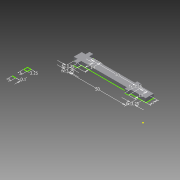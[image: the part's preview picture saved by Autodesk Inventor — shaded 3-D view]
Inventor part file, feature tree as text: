
AUTODESK INVENTOR PART (.ipt)
format: ipt  version: 2013 (Build 170138000, 138)  size: 106,496 bytes
history: native  units: mm
features: extrude x2, sketch x1
ambient origin geometry x8: Origin, YZ Plane, XZ Plane, XY Plane, X Axis, Y Axis, Z Axis, Center Point
feature tree (3):
  sketch  "Sketch1"  dims[d3=3.0mm d5=3.0mm d44=3.25mm d45=14.0mm d46=3.25mm d47=7.0mm d48=50.0mm d49=3.25mm d50=7.0mm d51=3.25mm d52=0.0mm d53=3.25mm d54=11.0mm d55=40.0mm d56=3.25mm d57=0.0mm]
  extrude  "Extrusion6"  Depth=3.0mm
  extrude  "Extrusion7"  Depth=3.25mm
